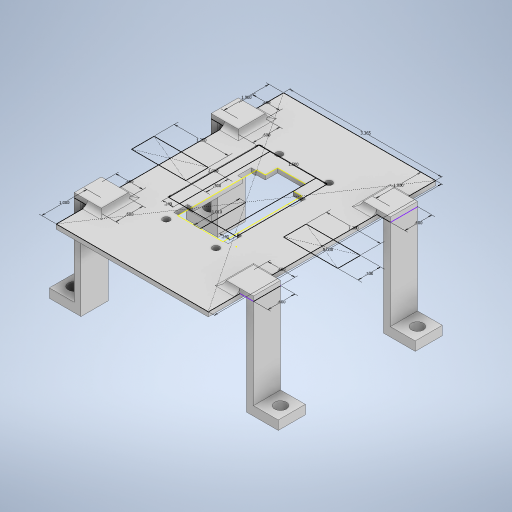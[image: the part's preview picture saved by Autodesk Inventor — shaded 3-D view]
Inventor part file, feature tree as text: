
AUTODESK INVENTOR PART (.ipt)
format: ipt  version: 2024.1 (Build 281209000, 209)  size: 556,032 bytes
history: native  units: in
note: dims shown in document units (in); Inventor stores cm internally (conversion verified against a paired STEP export)
features: extrude x11, sketch x11, projected_geometry x6, hole x3, fillet x2
ambient origin geometry x8: Origin, YZ Plane, XZ Plane, XY Plane, X Axis, Y Axis, Z Axis, Center Point
bodies: Solid1 (feature_tree)
feature tree (33):
  extrude  "Extrusion1"  Depth=2.0in
  extrude  "Extrusion2"  Depth=0.24in
  hole  "Hole1"  [1 undecoded]
  extrude  "Extrusion3"  Depth=1.0in TaperAngle=0.0deg
  extrude  "Extrusion4"  Depth=0.62in
  extrude  "Extrusion5"  Depth=2.02in
  sketch  "Sketch8"  dims[d18=0.5in d19=0.0in d20=0.62in]
  extrude  "Extrusion6"  Depth=1.75in
  sketch  "Sketch6"  dims[d8=0.5in]
  hole  "Hole2"  [1 undecoded]
  fillet  "Fillet1"  Radius=0.25in
  extrude  "Extrusion7"  Depth=0.2in
  extrude  "Extrusion8"  Depth=1.0in
  extrude  "Extrusion9"  Depth=0.2in
  fillet  "Fillet2"  Radius=0.125in
  extrude  "Extrusion10"  Depth=1.0in
  extrude  "Extrusion12"  Depth=3.3654in
  hole  "Hole4"  [1 undecoded]
  sketch  "Sketch3"  dims[d0=1.5in d1=2.0in]
  projected_geometry  "Projected Loop1"
  sketch  "Sketch4"  dims[d2=0.24in d3=0.24in]
  projected_geometry  "Projected Loop2"
  sketch  "Sketch5"  dims[d4=1.0in d5=0.0in d6=0.2in d7=0.0in]
  sketch  "Sketch7"  dims[d9=0.266in d10=0.75in d11=0.438in d12=0.25in d13=0.5635in d14=1.0in d15=0.8108in d16=0.5in d17=0.0in]
  projected_geometry  "Projected Loop3"
  sketch  "Sketch9"  dims[d21=2.02in d22=0.5in]
  sketch  "Sketch10"  dims[d23=1.75in d24=0.5in]
  sketch  "Sketch12"  dims[d25=0.1in d26=0.0in d27=0.2in d28=0.25in]
  sketch  "Sketch16"  dims[d29=0.2in d30=0.25in]
  projected_geometry  "Projected Loop4"
  projected_geometry  "Projected Loop5"
  projected_geometry  "Projected Loop6"
  sketch  "Sketch17"  dims[d31=0.2in d32=0.25in d33=0.2in d34=0.1495in d35=0.75in d36=0.375in d37=0.25in d38=0.5635in d39=1.0in d40=0.8108in d41=0.125in d42=1.01in d43=3.3654in d44=5.0299in d45=0.1in d46=0.0in d47=0.0in d48=0.0in d49=0.17in d50=0.17in d51=0.2in d52=0.3in d53=0.2in d54=0.3in d55=0.2in d56=0.3in d57=0.2in d58=0.3in d59=1.0in d60=0.0in d61=1.2in d62=0.5in d63=1.2in d64=0.5in d76=0.1in d77=0.0in d78=0.125in d79=1.0in d80=1.0in d81=1.0in d82=0.6in d83=0.6in d84=0.6in d85=0.6in d86=0.6in d87=0.6in d88=0.6in d89=2.0in d90=0.0in d95=0.7in d96=0.6in d97=0.7in d98=0.7in d99=0.7in d100=0.2in d101=0.0in d102=0.25in d103=0.25in d104=0.266in d105=0.75in d106=0.438in d107=0.25in d108=0.5635in d109=1.0in d110=0.8108in]
note: 3 required parameter values undecoded (feature->parameter linkage not recoverable at this tier; creation-order binding heuristic only, values carry confidence <= 0.55)
